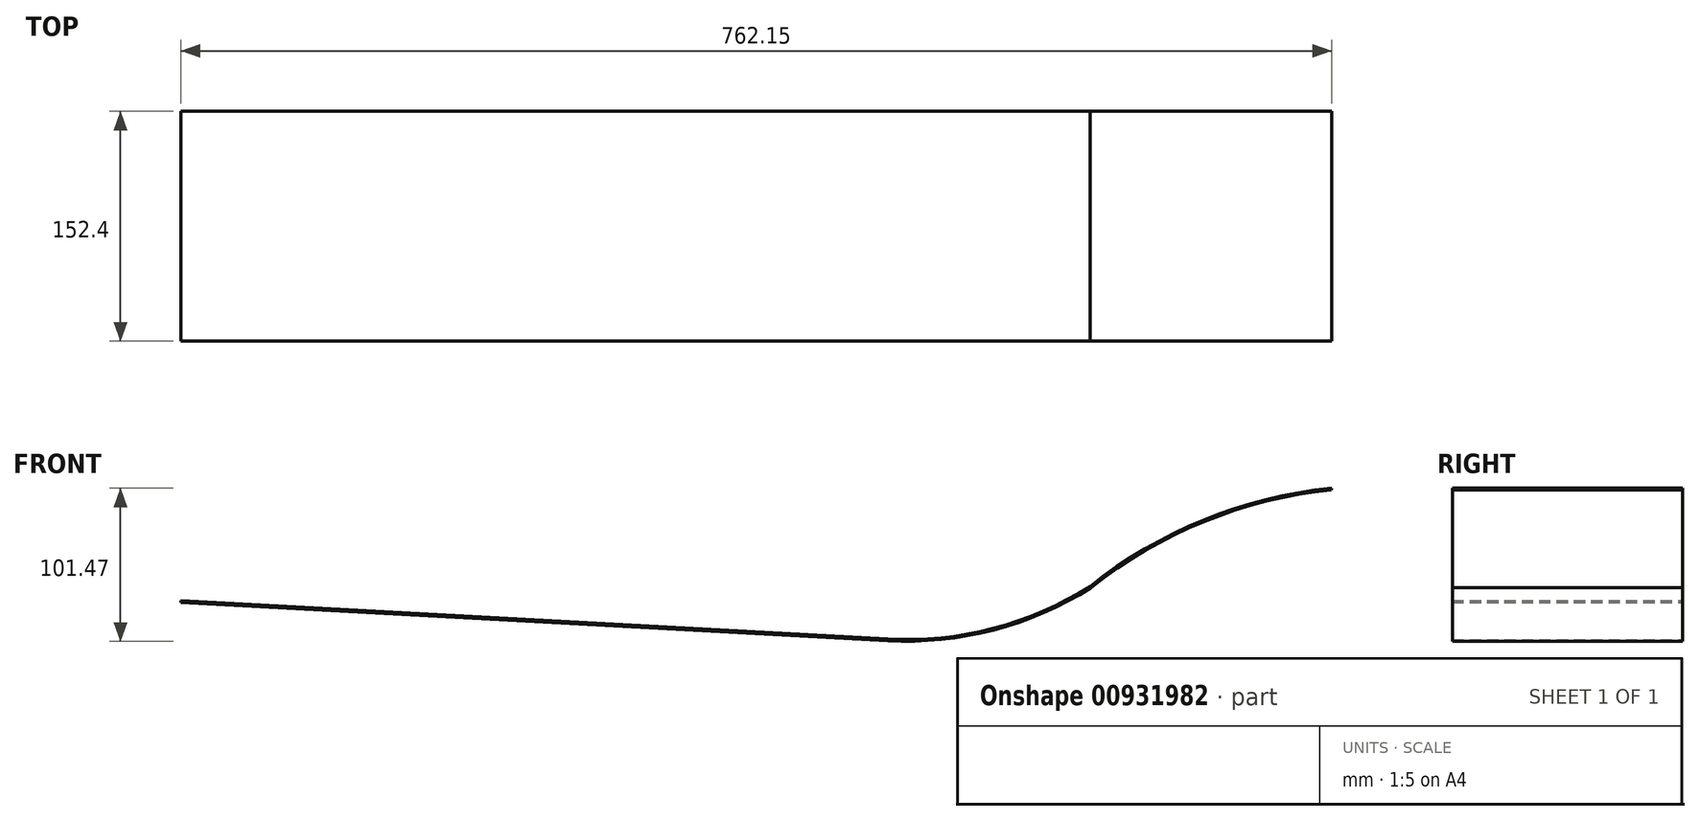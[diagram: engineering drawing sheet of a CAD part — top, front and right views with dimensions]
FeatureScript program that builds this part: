
annotation { "Feature Type Name" : "Feature", "Feature Type Description" : "" }
export const myFeature = defineFeature(function(context is Context, id is Id, definition is map)
    precondition{}
    {
        {
            var Q0;
            Q0=qCreatedBy(makeId("Front.planeOp"),FACE);
            var sketch = newSketch(context, id + "F0", { "sketchPlane" : qUnion([Q0])});
            skLineSegment(sketch, "E0", {"start": v(-145.39, 0) * mm, "end": v(217.21, 0) * mm, "construction": true});
            skLineSegment(sketch, "E1", {"start": v(-202.24, 177.8) * mm, "end": v(265.9, 152.4) * mm});
            skLineSegment(sketch, "E2", {"start": v(246.56, 152.4) * mm, "end": v(2.38, 152.4) * mm, "construction": true});
            skPoint(sketch, "E3.visualSharp", {"position": v(265.9, 152.4) * mm});
            skArc(sketch, "E3.filletArc", {"start": v(265.9, 152.4) * mm, "mid": v(335.92, 159.45) * mm, "end": v(400.49, 187.47) * mm});
            skPoint(sketch, "E4.visualSharp", {"position": v(334.76, 120.36) * mm});
            skArc(sketch, "E4.filletArc", {"start": v(559.76, 252.44) * mm, "mid": v(475.45, 231.42) * mm, "end": v(400.49, 187.47) * mm});
            skPoint(sketch, "E5.visualSharp", {"position": v(395.04, 386.6) * mm});
            skArc(sketch, "E6.0", {"start": v(559.91, 253.53) * mm, "mid": v(475.2, 232.47) * mm, "end": v(399.87, 188.34) * mm});
            skArc(sketch, "E6.1", {"start": v(265.95, 153.47) * mm, "mid": v(335.63, 160.48) * mm, "end": v(399.87, 188.34) * mm});
            skLineSegment(sketch, "E6.2", {"start": v(-202.17, 178.86) * mm, "end": v(265.95, 153.47) * mm});
            skLineSegment(sketch, "E7", {"start": v(-202.24, 177.8) * mm, "end": v(-202.17, 178.86) * mm});
            skLineSegment(sketch, "E8", {"start": v(559.76, 252.44) * mm, "end": v(559.91, 253.53) * mm});
            skSolve(sketch);
        }
        {
            var Q0;
            Q0 = qSketchRegion(id + "F0", true);
            extrude(context, id + "F1", {"entities" : qUnion([Q0]), "depth" : 76.2 * mm, "offsetDistance" : 25.4 * mm, "hasSecondDirection" : true, "secondDirectionOppositeDirection" : true, "secondDirectionDepth" : 76.2 * mm});
        }
    });
